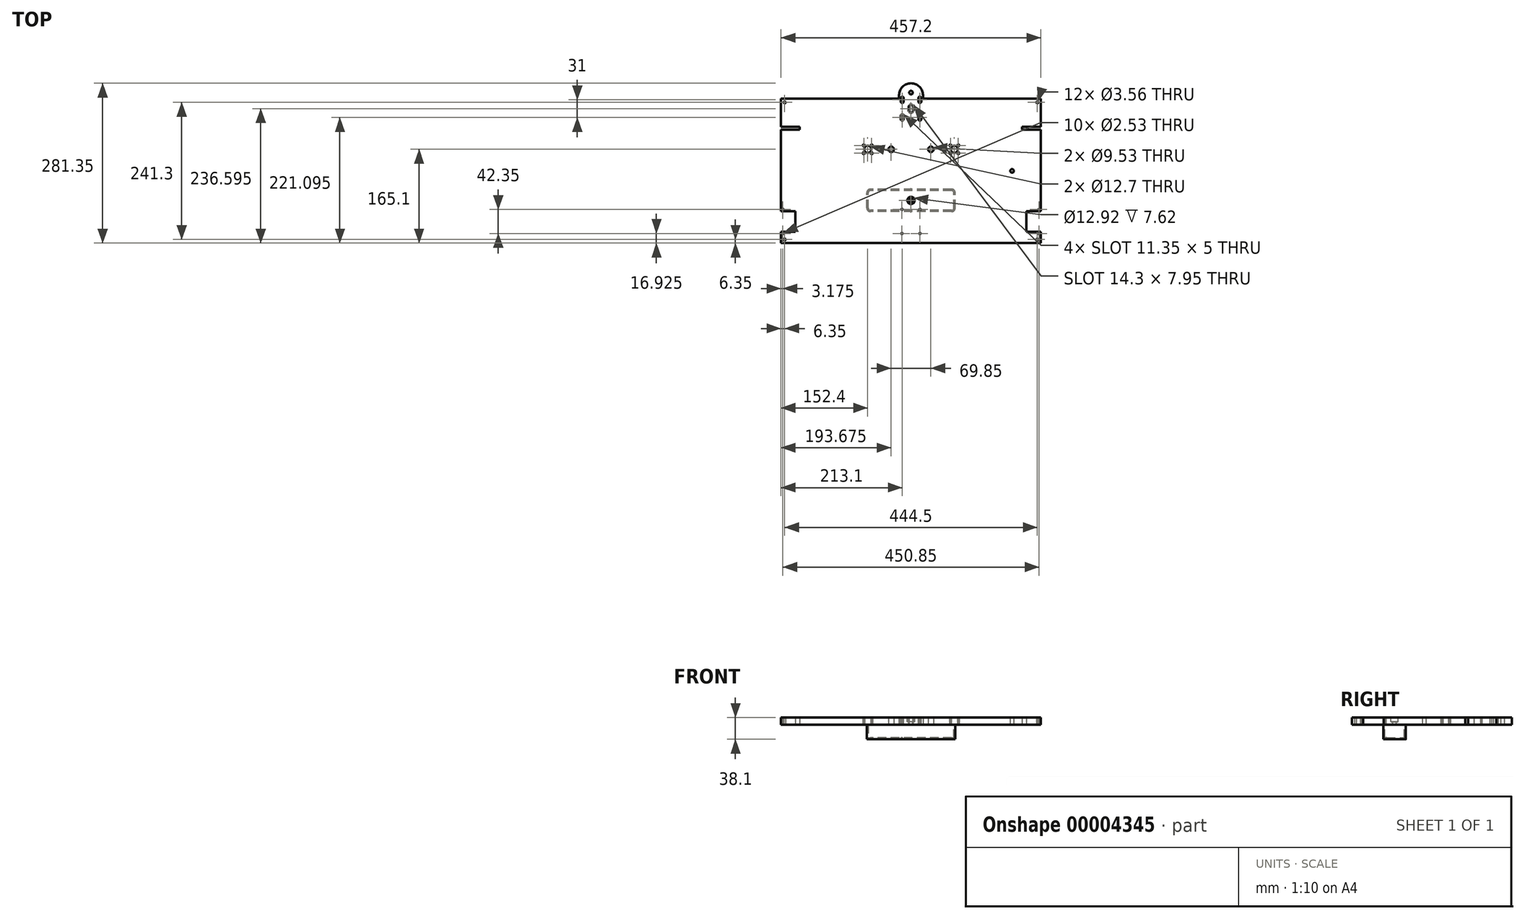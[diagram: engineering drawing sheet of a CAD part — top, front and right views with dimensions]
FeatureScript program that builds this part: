
annotation { "Feature Type Name" : "Feature", "Feature Type Description" : "" }
export const myFeature = defineFeature(function(context is Context, id is Id, definition is map)
    precondition{}
    {
        {
            var Q0;
            Q0=qCreatedBy(makeId("Top.planeOp"),FACE);
            var sketch = newSketch(context, id + "F0", { "sketchPlane" : qUnion([Q0])});
            skLineSegment(sketch, "E0", {"start": v(0, 0) * mm, "end": v(457.2, 0) * mm});
            skLineSegment(sketch, "E1", {"start": v(457.2, 0) * mm, "end": v(457.2, -254) * mm});
            skLineSegment(sketch, "E2", {"start": v(457.2, -254) * mm, "end": v(0, -254) * mm});
            skLineSegment(sketch, "E3", {"start": v(0, -254) * mm, "end": v(0, 0) * mm});
            skCircle(sketch, "E4", {"center": v(152.4, -88.9) * mm, "radius": 6.35 * mm});
            skLineSegment(sketch, "E5", {"start": v(152.4, -88.9) * mm, "end": v(304.8, -88.9) * mm, "construction": true});
            skCircle(sketch, "E6", {"center": v(304.8, -88.9) * mm, "radius": 6.35 * mm});
            skLineSegment(sketch, "E7", {"start": v(228.6, -88.9) * mm, "end": v(228.6, 0) * mm, "construction": true});
            skCircle(sketch, "E8", {"center": v(193.68, -88.9) * mm, "radius": 4.76 * mm});
            skCircle(sketch, "E9", {"center": v(263.53, -88.9) * mm, "radius": 4.76 * mm});
            skLineSegment(sketch, "E10", {"start": v(228.6, -88.9) * mm, "end": v(228.6, -254) * mm, "construction": true});
            skPoint(sketch, "E11", {"position": v(457.2, -215.9) * mm});
            skPoint(sketch, "E12", {"position": v(0, -215.9) * mm});
            skLineSegment(sketch, "E13", {"start": v(457.2, -215.9) * mm, "end": v(0, -215.9) * mm, "construction": true});
            skLineSegment(sketch, "E14.rect.bottom", {"start": v(431.8, -233.9) * mm, "end": v(457.2, -233.9) * mm});
            skLineSegment(sketch, "E14.rect.top", {"start": v(431.8, -197.9) * mm, "end": v(457.2, -197.9) * mm});
            skLineSegment(sketch, "E14.rect.left", {"start": v(431.8, -233.9) * mm, "end": v(431.8, -197.9) * mm});
            skLineSegment(sketch, "E14.rect.right", {"start": v(457.2, -233.9) * mm, "end": v(457.2, -197.9) * mm});
            skPoint(sketch, "E14.rect.middle", {"position": v(444.5, -215.9) * mm});
            skLineSegment(sketch, "E15.0.MirrorCS", {"start": v(25.4, -233.9) * mm, "end": v(25.4, -197.9) * mm});
            skLineSegment(sketch, "E16.0.MirrorCS", {"start": v(25.4, -197.9) * mm, "end": v(0, -197.9) * mm});
            skLineSegment(sketch, "E17.0.MirrorCS", {"start": v(0, -233.9) * mm, "end": v(0, -197.9) * mm});
            skLineSegment(sketch, "E18.0.MirrorCS", {"start": v(25.4, -233.9) * mm, "end": v(0, -233.9) * mm});
            skLineSegment(sketch, "E19.rect.bottom", {"start": v(300.03, -198.69) * mm, "end": v(157.17, -198.69) * mm});
            skLineSegment(sketch, "E19.rect.top", {"start": v(300.03, -159.01) * mm, "end": v(157.17, -159.01) * mm});
            skLineSegment(sketch, "E19.rect.left", {"start": v(306.38, -192.34) * mm, "end": v(306.38, -165.36) * mm});
            skLineSegment(sketch, "E19.rect.right", {"start": v(150.82, -192.34) * mm, "end": v(150.82, -165.36) * mm});
            skPoint(sketch, "E19.rect.middle", {"position": v(228.6, -178.85) * mm});
            skPoint(sketch, "E20.visualSharp", {"position": v(150.82, -159.01) * mm});
            skArc(sketch, "E20.filletArc", {"start": v(157.17, -159.01) * mm, "mid": v(152.68, -160.87) * mm, "end": v(150.82, -165.36) * mm});
            skPoint(sketch, "E21.visualSharp", {"position": v(150.82, -198.69) * mm});
            skArc(sketch, "E21.filletArc", {"start": v(150.82, -192.34) * mm, "mid": v(152.68, -196.83) * mm, "end": v(157.17, -198.69) * mm});
            skPoint(sketch, "E22.visualSharp", {"position": v(306.38, -198.69) * mm});
            skArc(sketch, "E22.filletArc", {"start": v(300.03, -198.69) * mm, "mid": v(304.52, -196.83) * mm, "end": v(306.38, -192.34) * mm});
            skPoint(sketch, "E23.visualSharp", {"position": v(306.38, -159.01) * mm});
            skArc(sketch, "E23.filletArc", {"start": v(306.38, -165.36) * mm, "mid": v(304.52, -160.87) * mm, "end": v(300.03, -159.01) * mm});
            skLineSegment(sketch, "E24.rect.bottom", {"start": v(311.71, -95.81) * mm, "end": v(297.89, -95.81) * mm, "construction": true});
            skLineSegment(sketch, "E24.rect.top", {"start": v(311.71, -81.99) * mm, "end": v(297.89, -81.99) * mm, "construction": true});
            skLineSegment(sketch, "E24.rect.left", {"start": v(311.71, -95.81) * mm, "end": v(311.71, -81.99) * mm, "construction": true});
            skLineSegment(sketch, "E24.rect.right", {"start": v(297.89, -95.81) * mm, "end": v(297.89, -81.99) * mm, "construction": true});
            skCircle(sketch, "E25", {"center": v(297.89, -81.99) * mm, "radius": 1.78 * mm});
            skCircle(sketch, "E26", {"center": v(311.71, -81.99) * mm, "radius": 1.78 * mm});
            skCircle(sketch, "E27", {"center": v(311.71, -95.81) * mm, "radius": 1.78 * mm});
            skCircle(sketch, "E28", {"center": v(297.89, -95.81) * mm, "radius": 1.78 * mm});
            skLineSegment(sketch, "E29.rect.left", {"start": v(159.31, -95.81) * mm, "end": v(159.31, -81.99) * mm, "construction": true});
            skCircle(sketch, "E30", {"center": v(145.49, -81.99) * mm, "radius": 1.78 * mm});
            skLineSegment(sketch, "E29.rect.top", {"start": v(159.31, -81.99) * mm, "end": v(145.49, -81.99) * mm, "construction": true});
            skCircle(sketch, "E31", {"center": v(145.49, -95.81) * mm, "radius": 1.78 * mm});
            skLineSegment(sketch, "E29.rect.right", {"start": v(145.49, -95.81) * mm, "end": v(145.49, -81.99) * mm, "construction": true});
            skCircle(sketch, "E32", {"center": v(159.31, -95.81) * mm, "radius": 1.78 * mm});
            skLineSegment(sketch, "E29.rect.bottom", {"start": v(159.31, -95.81) * mm, "end": v(145.49, -95.81) * mm, "construction": true});
            skCircle(sketch, "E33", {"center": v(159.31, -81.99) * mm, "radius": 1.78 * mm});
            skLineSegment(sketch, "E34", {"start": v(145.49, -95.81) * mm, "end": v(159.31, -81.99) * mm, "construction": true});
            skLineSegment(sketch, "E35.bottom", {"start": v(457.2, -254) * mm, "end": v(444.5, -254) * mm, "construction": true});
            skLineSegment(sketch, "E35.top", {"start": v(457.2, -241.3) * mm, "end": v(444.5, -241.3) * mm, "construction": true});
            skLineSegment(sketch, "E35.left", {"start": v(457.2, -254) * mm, "end": v(457.2, -241.3) * mm, "construction": true});
            skLineSegment(sketch, "E35.right", {"start": v(444.5, -254) * mm, "end": v(444.5, -241.3) * mm, "construction": true});
            skPoint(sketch, "E36", {"position": v(450.85, -247.65) * mm});
            skLineSegment(sketch, "E37", {"start": v(444.5, -254) * mm, "end": v(457.2, -241.3) * mm, "construction": true});
            skCircle(sketch, "E38", {"center": v(450.85, -247.65) * mm, "radius": 1.78 * mm});
            skLineSegment(sketch, "E39.top", {"start": v(457.2, 0) * mm, "end": v(444.5, 0) * mm, "construction": true});
            skLineSegment(sketch, "E39.right", {"start": v(444.5, -12.7) * mm, "end": v(444.5, 0) * mm, "construction": true});
            skLineSegment(sketch, "E39.bottom", {"start": v(457.2, -12.7) * mm, "end": v(444.5, -12.7) * mm, "construction": true});
            skPoint(sketch, "E40", {"position": v(450.85, -6.35) * mm});
            skLineSegment(sketch, "E41", {"start": v(444.5, -12.7) * mm, "end": v(457.2, 0) * mm, "construction": true});
            skCircle(sketch, "E42", {"center": v(450.85, -6.35) * mm, "radius": 1.78 * mm});
            skLineSegment(sketch, "E39.left", {"start": v(457.2, -12.7) * mm, "end": v(457.2, 0) * mm, "construction": true});
            skLineSegment(sketch, "E43.top", {"start": v(12.7, 0) * mm, "end": v(0, 0) * mm, "construction": true});
            skLineSegment(sketch, "E43.right", {"start": v(0, -12.7) * mm, "end": v(0, 0) * mm, "construction": true});
            skLineSegment(sketch, "E43.bottom", {"start": v(12.7, -12.7) * mm, "end": v(0, -12.7) * mm, "construction": true});
            skPoint(sketch, "E44", {"position": v(6.35, -6.35) * mm});
            skLineSegment(sketch, "E45", {"start": v(0, -12.7) * mm, "end": v(12.7, 0) * mm, "construction": true});
            skCircle(sketch, "E46", {"center": v(6.35, -6.35) * mm, "radius": 1.78 * mm});
            skLineSegment(sketch, "E43.left", {"start": v(12.7, -12.7) * mm, "end": v(12.7, 0) * mm, "construction": true});
            skLineSegment(sketch, "E47.top", {"start": v(12.7, -241.3) * mm, "end": v(0, -241.3) * mm, "construction": true});
            skLineSegment(sketch, "E47.right", {"start": v(0, -254) * mm, "end": v(0, -241.3) * mm, "construction": true});
            skLineSegment(sketch, "E47.bottom", {"start": v(12.7, -254) * mm, "end": v(0, -254) * mm, "construction": true});
            skPoint(sketch, "E48", {"position": v(6.35, -247.65) * mm});
            skLineSegment(sketch, "E49", {"start": v(0, -254) * mm, "end": v(12.7, -241.3) * mm, "construction": true});
            skCircle(sketch, "E50", {"center": v(6.35, -247.65) * mm, "radius": 1.78 * mm});
            skLineSegment(sketch, "E47.left", {"start": v(12.7, -254) * mm, "end": v(12.7, -241.3) * mm, "construction": true});
            skLineSegment(sketch, "E51.bottom", {"start": v(0, -49.4) * mm, "end": v(33.02, -49.4) * mm});
            skLineSegment(sketch, "E51.top", {"start": v(0, -54.48) * mm, "end": v(33.02, -54.48) * mm});
            skLineSegment(sketch, "E51.left", {"start": v(0, -49.4) * mm, "end": v(0, -54.48) * mm, "construction": true});
            skLineSegment(sketch, "E51.right", {"start": v(33.02, -49.4) * mm, "end": v(33.02, -54.48) * mm});
            skLineSegment(sketch, "E52.bottom", {"start": v(457.2, -49.4) * mm, "end": v(424.18, -49.4) * mm});
            skLineSegment(sketch, "E52.top", {"start": v(457.2, -54.48) * mm, "end": v(424.18, -54.48) * mm});
            skLineSegment(sketch, "E52.left", {"start": v(457.2, -49.4) * mm, "end": v(457.2, -54.48) * mm});
            skLineSegment(sketch, "E52.right", {"start": v(424.18, -49.4) * mm, "end": v(424.18, -54.48) * mm});
            skPoint(sketch, "E53", {"position": v(424.18, -51.94) * mm});
            skCircle(sketch, "E54", {"center": v(406.4, -127) * mm, "radius": 3.18 * mm});
            skCircle(sketch, "E55", {"center": v(228.6, 10.8) * mm, "radius": 3.18 * mm});
            skLineSegment(sketch, "E56", {"start": v(207.6, 6.35) * mm, "end": v(207.6, 0) * mm});
            skLineSegment(sketch, "E57", {"start": v(249.6, 6.35) * mm, "end": v(249.6, 0) * mm});
            skArc(sketch, "E58", {"start": v(249.6, 6.35) * mm, "mid": v(228.6, 27.35) * mm, "end": v(207.6, 6.35) * mm});
            skSolve(sketch);
        }
        {
            var Q0;
            {var subQ5=sQuery(id+"F0.wireOp",EDGE,"E0");Q0=makeQuery(id+"F0.imprint","IMPRINT",FACE,{"disambiguationData":[TD([[makeQuery(id+"F0.imprint","IMPRINT",EDGE,{"derivedFrom":subQ5}),-1.0]])]});}
            var Q1;
            Q1=makeQuery(id+"F0.imprint","IMPRINT",FACE,{"disambiguationData":[TD([[makeQuery(id+"F0.imprint","IMPRINT",EDGE,{"derivedFrom":sQuery(id+"F0.wireOp",EDGE,"E19.rect.bottom")}),-1.0]])]});
            var Q2;
            {var subQ0=sQuery(id+"F0.wireOp",EDGE,"a8195b3f-a36e-4fb4-8691-7d30bc8288c5");Q2=makeQuery(id+"F0.imprint","IMPRINT",FACE,{"disambiguationData":[TD([[makeQuery(id+"F0.imprint","IMPRINT",EDGE,{"derivedFrom":subQ0}),1.0]])]});}
            var Q3;
            Q3=makeQuery(id+"F0.imprint","IMPRINT",FACE,{"disambiguationData":[TD([[makeQuery(id+"F0.imprint","IMPRINT",EDGE,{"derivedFrom":sQuery(id+"F0.wireOp",EDGE,"E55")}),-1.0]])]});
            extrude(context, id + "F1", {"entities" : qUnion([Q0, Q1, Q2, Q3]), "depth" : 12.7 * mm});
        }
        {
            var Q0;
            Q0=makeQuery(id+"F1.opExtrude","CAP_FACE",FACE,{"disambiguationData":[OSD([sQuery(id+"F0.wireOp",EDGE,"E0"),sQuery(id+"F0.wireOp",EDGE,"E1"),sQuery(id+"F0.wireOp",EDGE,"E2"),sQuery(id+"F0.wireOp",EDGE,"E3"),sQuery(id+"F0.wireOp",EDGE,"E4"),sQuery(id+"F0.wireOp",EDGE,"E6"),sQuery(id+"F0.wireOp",EDGE,"E8"),sQuery(id+"F0.wireOp",EDGE,"E9"),sQuery(id+"F0.wireOp",EDGE,"12e8ddb0-5c58-4e96-90b9-ac8b6edad29a"),sQuery(id+"F0.wireOp",EDGE,"bb5e756b-0d9b-4ba5-8c97-108f7f482b33.left"),sQuery(id+"F0.wireOp",EDGE,"bb5e756b-0d9b-4ba5-8c97-108f7f482b33.right"),sQuery(id+"F0.wireOp",EDGE,"6a552e1d-9a3f-4ab7-9870-60ebdf4c9ddb.left"),sQuery(id+"F0.wireOp",EDGE,"6a552e1d-9a3f-4ab7-9870-60ebdf4c9ddb.right")])],"isStart":false});
            var sketch = newSketch(context, id + "F2", { "sketchPlane" : qUnion([Q0])});
            skCircle(sketch, "E59", {"center": v(228.6, -178.85) * mm, "radius": 6.46 * mm});
            skLineSegment(sketch, "E60", {"start": v(228.6, 0) * mm, "end": v(228.6, -254) * mm, "construction": true});
            skCircle(sketch, "E61", {"center": v(228.6, -178.85) * mm, "radius": 3.07 * mm});
            skLineSegment(sketch, "E62", {"start": v(0, -196.9) * mm, "end": v(0, -234.9) * mm, "construction": true});
            skPoint(sketch, "E63", {"position": v(0, -215.9) * mm});
            skCircle(sketch, "E64", {"center": v(228.6, -20.58) * mm, "radius": 11.88 * mm});
            skLineSegment(sketch, "E65.rect.bottom", {"start": v(213.1, -5.08) * mm, "end": v(244.1, -5.08) * mm, "construction": true});
            skLineSegment(sketch, "E65.rect.top", {"start": v(213.1, -36.08) * mm, "end": v(244.1, -36.08) * mm, "construction": true});
            skLineSegment(sketch, "E65.rect.left", {"start": v(213.1, -5.08) * mm, "end": v(213.1, -36.08) * mm, "construction": true});
            skLineSegment(sketch, "E65.rect.right", {"start": v(244.1, -5.08) * mm, "end": v(244.1, -36.08) * mm, "construction": true});
            skLineSegment(sketch, "E66", {"start": v(0, 0) * mm, "end": v(0, 0) * mm});
            skArc(sketch, "E67", {"start": v(210.6, -5.08) * mm, "mid": v(213.1, -7.58) * mm, "end": v(215.6, -5.08) * mm});
            skArc(sketch, "E68", {"start": v(215.6, 1.27) * mm, "mid": v(213.1, 3.77) * mm, "end": v(210.6, 1.27) * mm});
            skLineSegment(sketch, "E69", {"start": v(210.6, 1.27) * mm, "end": v(210.6, -5.08) * mm});
            skLineSegment(sketch, "E70", {"start": v(215.6, -5.08) * mm, "end": v(215.6, 1.27) * mm});
            skArc(sketch, "E71", {"start": v(210.6, -36.08) * mm, "mid": v(213.1, -38.58) * mm, "end": v(215.6, -36.08) * mm});
            skArc(sketch, "E72", {"start": v(215.6, -29.73) * mm, "mid": v(213.1, -27.23) * mm, "end": v(210.6, -29.73) * mm});
            skLineSegment(sketch, "E73", {"start": v(210.6, -29.73) * mm, "end": v(210.6, -36.08) * mm});
            skLineSegment(sketch, "E74", {"start": v(215.6, -36.08) * mm, "end": v(215.6, -29.73) * mm});
            skArc(sketch, "E75", {"start": v(241.6, -5.08) * mm, "mid": v(244.1, -7.58) * mm, "end": v(246.6, -5.08) * mm});
            skArc(sketch, "E76", {"start": v(246.6, 1.27) * mm, "mid": v(244.1, 3.77) * mm, "end": v(241.6, 1.27) * mm});
            skLineSegment(sketch, "E77", {"start": v(241.6, 1.27) * mm, "end": v(241.6, -5.08) * mm});
            skLineSegment(sketch, "E78", {"start": v(246.6, -5.08) * mm, "end": v(246.6, 1.27) * mm});
            skArc(sketch, "E79", {"start": v(241.6, -36.08) * mm, "mid": v(244.1, -38.58) * mm, "end": v(246.6, -36.08) * mm});
            skArc(sketch, "E80", {"start": v(246.6, -29.73) * mm, "mid": v(244.1, -27.23) * mm, "end": v(241.6, -29.73) * mm});
            skLineSegment(sketch, "E81", {"start": v(241.6, -29.73) * mm, "end": v(241.6, -36.08) * mm});
            skLineSegment(sketch, "E82", {"start": v(246.6, -36.08) * mm, "end": v(246.6, -29.73) * mm});
            skLineSegment(sketch, "E83", {"start": v(232.58, -14.23) * mm, "end": v(232.58, -20.58) * mm});
            skLineSegment(sketch, "E84", {"start": v(224.62, -20.58) * mm, "end": v(224.62, -14.23) * mm});
            skArc(sketch, "E85", {"start": v(232.58, -14.23) * mm, "mid": v(228.6, -10.25) * mm, "end": v(224.62, -14.23) * mm});
            skArc(sketch, "E86", {"start": v(224.62, -20.58) * mm, "mid": v(228.6, -24.56) * mm, "end": v(232.58, -20.58) * mm});
            skSolve(sketch);
        }
        {
            var Q0;
            Q0=makeQuery(id+"F2.imprint","IMPRINT",FACE,{"disambiguationData":[TD([[makeQuery(id+"F2.imprint","IMPRINT",EDGE,{"derivedFrom":sQuery(id+"F2.wireOp",EDGE,"E61")}),1.0]])]});
            extrude(context, id + "F3", {"entities" : qUnion([Q0]), "operationType" : NewBodyOperationType.REMOVE, "endBound" : BoundingType.UP_TO_NEXT, "oppositeDirection" : true, "depth" : 25.4 * mm});
        }
        {
            var Q0;
            Q0=makeQuery(id+"F2.imprint","IMPRINT",FACE,{"disambiguationData":[TD([[makeQuery(id+"F2.imprint","IMPRINT",EDGE,{"derivedFrom":sQuery(id+"F2.wireOp",EDGE,"E59")}),1.0]])]});
            extrude(context, id + "F4", {"entities" : qUnion([Q0]), "operationType" : NewBodyOperationType.REMOVE, "oppositeDirection" : true, "depth" : 7.62 * mm});
        }
        {
            var Q0;
            Q0=makeQuery(id+"F2.imprint","IMPRINT",FACE,{"disambiguationData":[TD([[makeQuery(id+"F2.imprint","IMPRINT",EDGE,{"derivedFrom":sQuery(id+"F2.wireOp",EDGE,"e866b2c7-b09f-4727-805e-bbe1f4ddcb7b")}),1.0]])]});
            var Q1;
            Q1=makeQuery(id+"F2.imprint","IMPRINT",FACE,{"disambiguationData":[TD([[makeQuery(id+"F2.imprint","IMPRINT",EDGE,{"derivedFrom":sQuery(id+"F2.wireOp",EDGE,"5cfc62ed-0796-424f-afe6-3ee8251b4bd1")}),1.0]])]});
            var Q2;
            Q2=makeQuery(id+"F2.imprint","IMPRINT",FACE,{"disambiguationData":[TD([[makeQuery(id+"F2.imprint","IMPRINT",EDGE,{"derivedFrom":sQuery(id+"F2.wireOp",EDGE,"2405e6e9-40c9-4f32-a162-f9d9b48d3703")}),1.0]])]});
            var Q3;
            Q3=makeQuery(id+"F2.imprint","IMPRINT",FACE,{"disambiguationData":[TD([[makeQuery(id+"F2.imprint","IMPRINT",EDGE,{"derivedFrom":sQuery(id+"F2.wireOp",EDGE,"b2eefeab-9059-4bb7-8fc5-a07396598a16")}),1.0]])]});
            var Q4;
            Q4=makeQuery(id+"F2.imprint","IMPRINT",FACE,{"disambiguationData":[TD([[makeQuery(id+"F2.imprint","IMPRINT",EDGE,{"derivedFrom":sQuery(id+"F2.wireOp",EDGE,"e3809f3d-2206-4c3c-b2f2-a941fb980214")}),1.0]])]});
            var Q5;
            Q5=makeQuery(id+"F2.imprint","IMPRINT",FACE,{"disambiguationData":[TD([[makeQuery(id+"F2.imprint","IMPRINT",EDGE,{"derivedFrom":sQuery(id+"F2.wireOp",EDGE,"E71")}),1.0]])]});
            var Q6;
            Q6=makeQuery(id+"F2.imprint","IMPRINT",FACE,{"disambiguationData":[TD([[makeQuery(id+"F2.imprint","IMPRINT",EDGE,{"derivedFrom":sQuery(id+"F2.wireOp",EDGE,"E67")}),1.0]])]});
            var Q7;
            Q7=makeQuery(id+"F2.imprint","IMPRINT",FACE,{"disambiguationData":[TD([[makeQuery(id+"F2.imprint","IMPRINT",EDGE,{"derivedFrom":sQuery(id+"F2.wireOp",EDGE,"E75")}),1.0]])]});
            var Q8;
            Q8=makeQuery(id+"F2.imprint","IMPRINT",FACE,{"disambiguationData":[TD([[makeQuery(id+"F2.imprint","IMPRINT",EDGE,{"derivedFrom":sQuery(id+"F2.wireOp",EDGE,"E79")}),1.0]])]});
            var Q9;
            Q9=makeQuery(id+"F2.imprint","IMPRINT",FACE,{"disambiguationData":[TD([[makeQuery(id+"F2.imprint","IMPRINT",EDGE,{"derivedFrom":sQuery(id+"F2.wireOp",EDGE,"E83")}),-1.0]])]});
            extrude(context, id + "F5", {"entities" : qUnion([Q0, Q1, Q2, Q3, Q4, Q5, Q6, Q7, Q8, Q9]), "operationType" : NewBodyOperationType.REMOVE, "endBound" : BoundingType.UP_TO_NEXT, "oppositeDirection" : true, "depth" : 25.4 * mm});
        }
        {
            var Q0;
            Q0=makeQuery(id+"F0.imprint","IMPRINT",FACE,{"disambiguationData":[TD([[makeQuery(id+"F0.imprint","IMPRINT",EDGE,{"derivedFrom":sQuery(id+"F0.wireOp",EDGE,"E19.rect.bottom")}),-1.0]])]});
            extrude(context, id + "F6", {"entities" : qUnion([Q0]), "oppositeDirection" : true, "depth" : 25.4 * mm});
        }
        {
            var Q0;
            Q0=makeQuery(id+"F6.opExtrude","CAP_FACE",FACE,{"disambiguationData":[OSD([sQuery(id+"F0.wireOp",EDGE,"E19.rect.bottom"),sQuery(id+"F0.wireOp",EDGE,"E19.rect.top"),sQuery(id+"F0.wireOp",EDGE,"E19.rect.left"),sQuery(id+"F0.wireOp",EDGE,"E19.rect.right"),sQuery(id+"F0.wireOp",EDGE,"E20.filletArc"),sQuery(id+"F0.wireOp",EDGE,"E21.filletArc"),sQuery(id+"F0.wireOp",EDGE,"E22.filletArc"),sQuery(id+"F0.wireOp",EDGE,"E23.filletArc")])],"isStart":true});
            shell(context, id + "F7", {"entities" : qUnion([Q0]), "thickness" : 2.54 * mm});
        }
        {
            var Q0;
            Q0=makeQuery(id+"F2.imprint","IMPRINT",FACE,{"disambiguationData":[TD([[makeQuery(id+"F2.imprint","IMPRINT",EDGE,{"derivedFrom":sQuery(id+"F2.wireOp",EDGE,"E59")}),-1.0]])]});
            var sketch = newSketch(context, id + "F8", { "sketchPlane" : qUnion([Q0])});
            skPoint(sketch, "E87", {"position": v(0, -194.73) * mm});
            skPoint(sketch, "E88", {"position": v(0, -237.08) * mm});
            skLineSegment(sketch, "E89", {"start": v(0, -194.73) * mm, "end": v(457.2, -194.73) * mm, "construction": true});
            skLineSegment(sketch, "E90", {"start": v(0, -237.08) * mm, "end": v(457.2, -237.08) * mm, "construction": true});
            skPoint(sketch, "E91", {"position": v(212.73, -194.73) * mm});
            skPoint(sketch, "E92", {"position": v(212.73, -237.08) * mm});
            skPoint(sketch, "E93", {"position": v(454.03, -194.73) * mm});
            skPoint(sketch, "E94", {"position": v(454.03, -237.08) * mm});
            skPoint(sketch, "E95", {"position": v(244.48, -237.08) * mm});
            skPoint(sketch, "E96", {"position": v(244.48, -194.73) * mm});
            skPoint(sketch, "E97", {"position": v(3.17, -194.73) * mm});
            skPoint(sketch, "E98", {"position": v(3.18, -237.08) * mm});
            skCircle(sketch, "E99", {"center": v(3.17, -194.73) * mm, "radius": 1.26 * mm});
            skCircle(sketch, "E100", {"center": v(3.18, -237.08) * mm, "radius": 1.26 * mm});
            skCircle(sketch, "E101", {"center": v(212.73, -194.73) * mm, "radius": 1.26 * mm});
            skCircle(sketch, "E102", {"center": v(212.73, -237.08) * mm, "radius": 1.26 * mm});
            skCircle(sketch, "E103", {"center": v(244.48, -194.73) * mm, "radius": 1.26 * mm});
            skCircle(sketch, "E104", {"center": v(244.48, -237.08) * mm, "radius": 1.26 * mm});
            skCircle(sketch, "E105", {"center": v(454.03, -237.08) * mm, "radius": 1.26 * mm});
            skCircle(sketch, "E106", {"center": v(454.03, -194.73) * mm, "radius": 1.26 * mm});
            skSolve(sketch);
        }
        {
            var Q0;
            Q0 = qSketchRegion(id + "F8", true);
            extrude(context, id + "F9", {"entities" : qUnion([Q0]), "operationType" : NewBodyOperationType.REMOVE, "endBound" : BoundingType.THROUGH_ALL, "oppositeDirection" : true, "depth" : 25.4 * mm});
        }
    });
